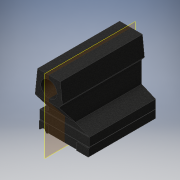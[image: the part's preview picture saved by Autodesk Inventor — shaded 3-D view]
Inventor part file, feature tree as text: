
AUTODESK INVENTOR PART (.ipt)
format: ipt  version: 2016 (Build 200138000, 138)  size: 423,936 bytes
history: native  units: mm
features: extrude x26, sketch x26, fillet x6, plane x2
ambient origin geometry x8: Origin, YZ Plane, XZ Plane, XY Plane, X Axis, Y Axis, Z Axis, Center Point
bodies: Solid1 (feature_tree)
feature tree (60):
  extrude  "Extrusion1"  Depth=151.0mm
  extrude  "Extrusion2"  Depth=203.0mm
  extrude  "Extrusion3"  TaperAngle=135.0deg  [1 undecoded]
  extrude  "Extrusion4"  Depth=10.0mm
  extrude  "Extrusion5"  Depth=28.0mm
  extrude  "Extrusion6"  Depth=2.0mm TaperAngle=0.0deg
  fillet  "Fillet1"  Radius=37.0mm
  extrude  "Extrusion7"  Depth=1.0mm TaperAngle=0.0deg
  fillet  "Fillet3"  Radius=5.0mm
  extrude  "Extrusion8"  Depth=5.0mm
  extrude  "Extrusion9"  Depth=1.0mm
  extrude  "Extrusion10"  Depth=1.0mm
  extrude  "Extrusion11"  Depth=1.0mm TaperAngle=0.0deg
  plane  "Work Plane1"
  extrude  "Extrusion12"  Depth=49.0mm TaperAngle=0.0deg
  extrude  "Extrusion13"  Depth=35.0mm
  extrude  "Extrusion14"  Depth=16.755161mm
  extrude  "Extrusion15"  Depth=295.5mm TaperAngle=0.0deg
  fillet  "Fillet4"  Radius=295.5mm
  extrude  "Extrusion16"  Depth=295.5mm TaperAngle=0.0deg
  extrude  "Extrusion17"  Depth=2.0mm
  plane  "Work Plane2"
  extrude  "Extrusion18"  Depth=50.0mm
  extrude  "Extrusion19"  Depth=5.0mm TaperAngle=0.0deg
  extrude  "Extrusion20"  Depth=1.0mm TaperAngle=0.0deg
  extrude  "Extrusion21"  Depth=207.0mm TaperAngle=0.0deg
  extrude  "Extrusion22"  Depth=204.0mm
  extrude  "Extrusion23"  Depth=6.981317mm
  extrude  "Extrusion24"  Depth=204.0mm TaperAngle=0.0deg
  fillet  "Fillet5"  Radius=25.3mm
  fillet  "Fillet6"  Radius=3.0mm
  extrude  "Extrusion25"  Depth=3.0mm
  fillet  "Fillet7"  Radius=36.2mm
  extrude  "Extrusion26"  Depth=3.0mm
  sketch  "Sketch1"  dims[d19=26.0mm d20=151.0mm]
  sketch  "Sketch2"  dims[d21=203.0mm d22=0.0mm d23=28.0mm]
  sketch  "Sketch3"  dims[d29=4.0mm d30=135.0deg]
  sketch  "Sketch4"  dims[d31=45.0deg d32=10.0mm]
  sketch  "Sketch5"  dims[d33=215.0mm d34=0.0mm d35=28.0mm]
  sketch  "Sketch6"  dims[d36=6.0mm d37=0.0mm d38=2.0mm d39=0.0mm d40=37.0mm]
  sketch  "Sketch8"  dims[d41=6.0mm d42=0.0mm d43=1.0mm d44=0.0mm d45=5.0mm]
  sketch  "Sketch9"  dims[d47=1.0mm d48=0.0mm d49=5.0mm]
  sketch  "Sketch10"  dims[d50=1.0mm d51=1.0mm]
  sketch  "Sketch11"  dims[d52=1.0mm d53=1.0mm]
  sketch  "Sketch12"  dims[d54=1.0mm d55=0.0mm d56=26.0mm d57=0.0mm]
  sketch  "Sketch13"  dims[d58=49.0mm d59=152.0mm d60=0.0mm]
  sketch  "Sketch14"  dims[d61=35.0mm d62=35.0mm]
  sketch  "Sketch15"  dims[d63=16.755161mm d64=16.755161mm]
  sketch  "Sketch16"  dims[d65=58.0mm d66=295.5mm d67=0.0mm d68=295.5mm d69=0.0mm]
  sketch  "Sketch18"  dims[d70=295.5mm d71=0.0mm d72=295.5mm d73=0.0mm]
  sketch  "Sketch19"  dims[d74=1.0mm d75=0.0mm d76=2.0mm]
  sketch  "Sketch20"  dims[d85=1.0mm d86=0.0mm d87=50.0mm]
  sketch  "Sketch21"  dims[d88=300.0mm d89=0.0mm d90=5.0mm d91=0.0mm]
  sketch  "Sketch23"  dims[d92=1.0mm d93=0.0mm d94=1.0mm d95=0.0mm]
  sketch  "Sketch24"  dims[d96=2.0mm d97=207.0mm d98=0.0mm]
  sketch  "Sketch25"  dims[d99=204.0mm d100=0.0mm d101=148.124mm]
  sketch  "Sketch26"  dims[d102=10.2mm d103=6.981317mm]
  sketch  "Sketch27"  dims[d104=3.8mm d106=204.0mm d107=0.0mm d108=25.3mm d109=3.0mm d110=0.0mm]
  sketch  "Sketch28"  dims[d111=3.0mm d112=3.0mm d113=36.2mm]
  sketch  "Sketch29"  dims[d114=3.0mm d115=0.0mm d116=3.0mm d117=2.0mm d118=24.43461mm d121=4.0mm d122=8.0mm d123=22.68928mm d124=10.0mm d125=0.0mm]
note: 1 required parameter value undecoded (feature->parameter linkage not recoverable at this tier; creation-order binding heuristic only, values carry confidence <= 0.55)
